# Revit family: Colt
name_source: partatom
category: Мебель
revit_build: Autodesk Revit 2017 (Build: 20160225_1515(x64)
units: mm (PartAtom-declared; Revit-internal decimal feet)

## family parameters
Всегда вертикально = Да
На основе рабочей плоскости = Нет
Общий = Нет
При загрузке вырезать с полостями = Нет
Точка расчета площади = Нет

## types (30) — shared parameters
Material = Skandiform Wood Oak Veneer
Изготовитель = Skandiform AB
Ключевая пометка = XBE.1
Комментарии к типоразмеру = Created by Astacus AB

## per-type parameters (varying)
| type | Circler Top | Depth | In Side Depth | In Side Width | Left Legs Distance | Middle Legs | Radius | Rectangler Top | Right Legs Distance | URL | Width |
| HB-960 | Да | 500 мм | 440 мм | 440 мм | 220 мм | Нет | 600 мм | Нет | 220 мм | http://file-system.ru | 500 мм |
| HB-961 | Да | 500 мм | 522 мм | 522 мм | 261 мм | Нет | 700 мм | Нет | 261 мм | www.biminfo.se/?productid=333355 | 500 мм |
| HB-962 | Да | 500 мм | 606 мм | 606 мм | 303 мм | Нет | 800 мм | Нет | 303 мм | www.biminfo.se/?productid=333355 | 500 мм |
| HB-965 | Нет | 1000 мм | 440 мм | 440 мм | 220 мм | Нет | 500 мм | Да | 220 мм | www.biminfo.se/?productid=333355 | 1000 мм |
| HB-966 | Нет | 1000 мм | 440 мм | 1200 мм | 600 мм | Нет | 500 мм | Да | 600 мм | www.biminfo.se/?productid=333355 | 1800 мм |
| HB-967 | Нет | 1000 мм | 440 мм | 1800 мм | 900 мм | Нет | 500 мм | Да | 900 мм | www.biminfo.se/?productid=333355 | 2400 мм |
| HB-973 | Нет | 1200 мм | 640 мм | 640 мм | 320 мм | Нет | 500 мм | Да | 320 мм | www.biminfo.se/?productid=333355 | 1200 мм |
| HB-976 | Нет | 1200 мм | 640 мм | 1200 мм | 600 мм | Нет | 500 мм | Да | 600 мм | www.biminfo.se/?productid=333355 | 1800 мм |
| HB-977 | Нет | 1200 мм | 640 мм | 1800 мм | 900 мм | Нет | 500 мм | Да | 900 мм | www.biminfo.se/?productid=333355 | 2400 мм |
| HB-985 | Нет | 1400 мм | 840 мм | 840 мм | 420 мм | Нет | 500 мм | Да | 420 мм | www.biminfo.se/?productid=333355 | 1400 мм |
| HB-986 | Нет | 1400 мм | 840 мм | 1200 мм | 600 мм | Нет | 500 мм | Да | 600 мм | www.biminfo.se/?productid=333355 | 1800 мм |
| HB-1964 | Нет | 1000 мм | 440 мм | 2400 мм | 1200 мм | Да | 500 мм | Да | 1200 мм | www.biminfo.se/?productid=333355 | 3000 мм |
| HB-1964-1963 | Нет | 1000 мм | 440 мм | 3600 мм | 1200 мм | Да | 500 мм | Да | 1200 мм | www.biminfo.se/?productid=333355 | 4200 мм |
| HB-1964-1966 | Нет | 1000 мм | 440 мм | 4200 мм | 1200 мм | Да | 500 мм | Да | 1200 мм | www.biminfo.se/?productid=333355 | 4800 мм |
| HB-1969 | Нет | 1000 мм | 440 мм | 3600 мм | 1800 мм | Да | 500 мм | Да | 1800 мм | www.biminfo.se/?productid=333355 | 4200 мм |
| HB-1969-1963 | Нет | 1000 мм | 440 мм | 4800 мм | 1800 мм | Да | 500 мм | Да | 1800 мм | www.biminfo.se/?productid=333355 | 5400 мм |
| HB-1969-1966 | Нет | 1000 мм | 440 мм | 5400 мм | 1800 мм | Да | 500 мм | Да | 1800 мм | www.biminfo.se/?productid=333355 | 6000 мм |
| HB-1974 | Нет | 1200 мм | 640 мм | 2400 мм | 1200 мм | Да | 500 мм | Да | 1200 мм | www.biminfo.se/?productid=333355 | 3000 мм |
| HB-1974-1973 | Нет | 1200 мм | 640 мм | 3600 мм | 1200 мм | Да | 500 мм | Да | 1200 мм | www.biminfo.se/?productid=333355 | 4200 мм |
| HB-1974-1976 | Нет | 1200 мм | 640 мм | 4200 мм | 1200 мм | Да | 500 мм | Да | 1200 мм | www.biminfo.se/?productid=333355 | 4800 мм |
| HB-1979 | Нет | 1200 мм | 640 мм | 3600 мм | 1800 мм | Да | 500 мм | Да | 1800 мм | www.biminfo.se/?productid=333355 | 4200 мм |
| HB-1979-1973 | Нет | 1200 мм | 640 мм | 4800 мм | 1800 мм | Да | 500 мм | Да | 1800 мм | www.biminfo.se/?productid=333355 | 5400 мм |
| HB-1979-1976 | Нет | 1200 мм | 640 мм | 5400 мм | 1800 мм | Да | 500 мм | Да | 1800 мм | www.biminfo.se/?productid=333355 | 6000 мм |
| HB-1984 | Нет | 1400 мм | 840 мм | 2400 мм | 1200 мм | Да | 500 мм | Да | 1200 мм | www.biminfo.se/?productid=333355 | 3000 мм |
| HB-1984-1983 | Нет | 1400 мм | 840 мм | 3600 мм | 1200 мм | Да | 500 мм | Да | 1200 мм | www.biminfo.se/?productid=333355 | 4200 мм |
| HB-1984-1986 | Нет | 1400 мм | 840 мм | 4200 мм | 1200 мм | Да | 500 мм | Да | 1200 мм | www.biminfo.se/?productid=333355 | 4800 мм |
| HB-1989 | Нет | 1400 мм | 840 мм | 3600 мм | 1800 мм | Да | 500 мм | Да | 1800 мм | www.biminfo.se/?productid=333355 | 4200 мм |
| HB-1989-1983 | Нет | 1400 мм | 840 мм | 4800 мм | 1800 мм | Да | 500 мм | Да | 1800 мм | www.biminfo.se/?productid=333355 | 5400 мм |
| HB-1989-1986 | Нет | 1400 мм | 840 мм | 5400 мм | 1800 мм | Да | 500 мм | Да | 1800 мм | www.biminfo.se/?productid=333355 | 6000 мм |
| HB-987 | Нет | 1400 мм | 840 мм | 1800 мм | 900 мм | Нет | 500 мм | Да | 900 мм | www.biminfo.se/?productid=333355 | 2400 мм |

note: column(s) folded — value = type name in every type: Группа модели

## geometry (parser evidence)
native form markers: Blend x5, Sweep x2
no freeform markers — native parametric forms only
